# Revit family: QF_BOURGEAT_Chariot_multi_standard_Gastro_et_Pâtissier
name_source: partatom
category: Equipement spécialisé
revit_build: Autodesk Revit 2015 (Build: 20140606_1530(x64)
units: mm (PartAtom-declared; Revit-internal decimal feet)

## types (1)
- 10 niveaux - espacement 37 mm
    Barre renfort largeur = 555 mm  [stored 1.82087 ft]
    Barre renfort longueur = 415 mm  [stored 1.36155 ft]
    Certification = NF Hygiène Alimentaire
    Charge max = 200.00 kg
    Charge maxi = 20 kg par glissière
    Charge totale maxi = 200 kg par chariot
    Fabricant = BOURGEAT
    Hauteur echelle = 1487 mm  [stored 4.87861 ft]
    Hauteur hors tout = 1650 mm  [stored 5.41339 ft]
    Longueur hors tout = 540 mm  [stored 1.77165 ft]
    Modèle = 776510
    Niveaux = 10
    Norme = EN 631.2
    Poids net à vide = 33.00 kg
    Poids à vide = 33 kg
    Profondeur echelle = 605 mm  [stored 1.98491 ft]
    Profondeur hors tout = 680 mm  [stored 2.23097 ft]
    Spécification du Fabricant = Chariot multi-standard
    URL catalogue = http://www.bourgeat.fr

note: [stored X ft] marks values corroborated as IEEE doubles in the binary element streams (Revit-internal decimal feet)
